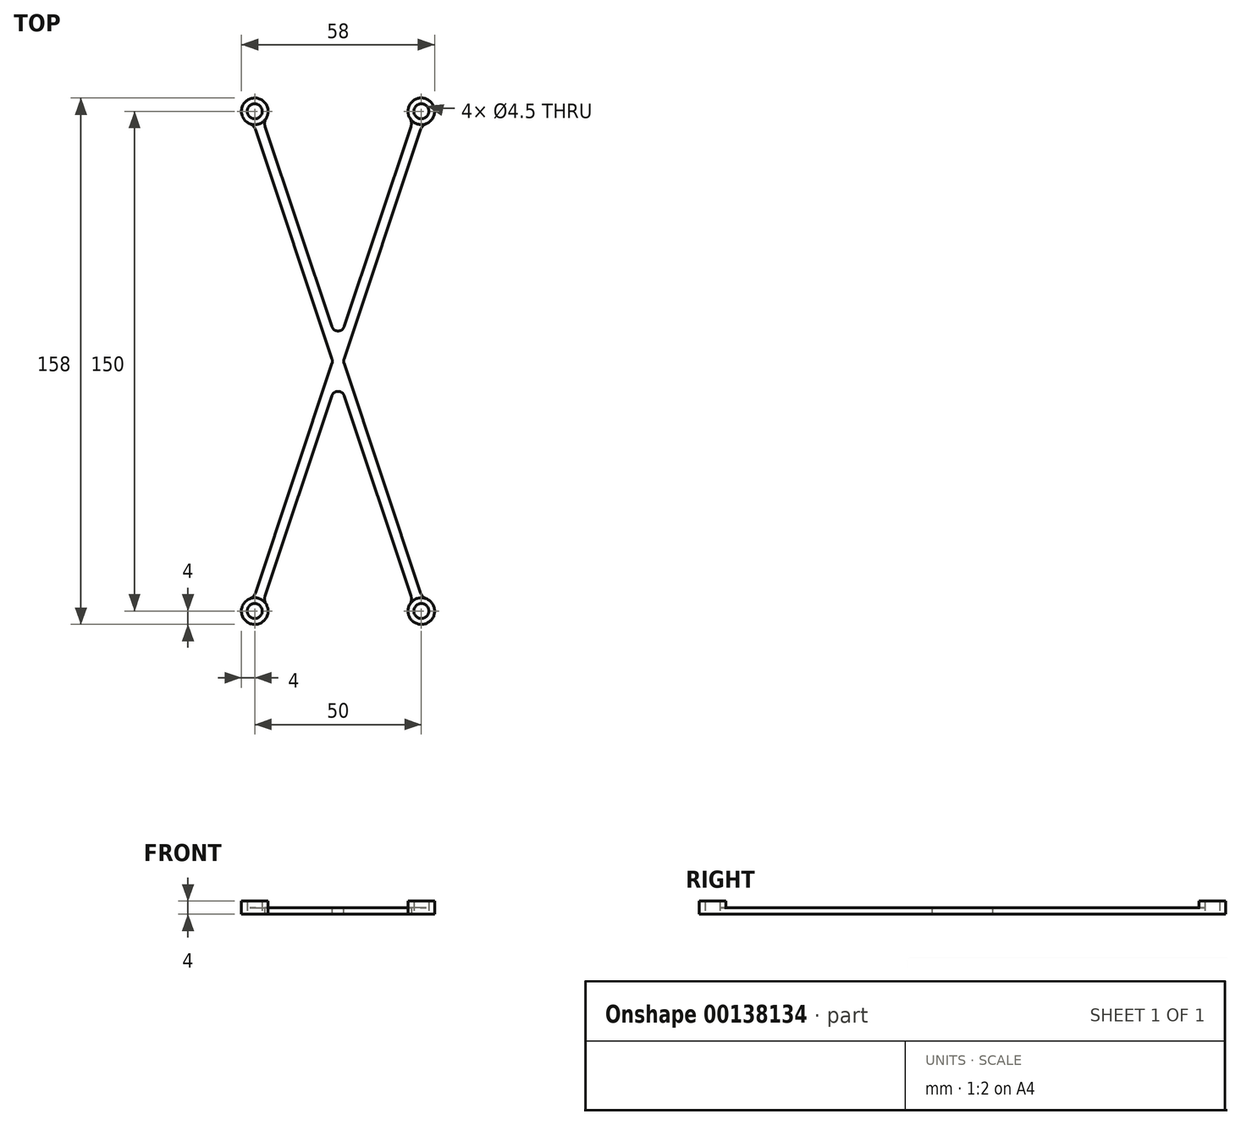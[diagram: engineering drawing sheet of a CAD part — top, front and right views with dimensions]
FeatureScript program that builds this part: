
annotation { "Feature Type Name" : "Feature", "Feature Type Description" : "" }
export const myFeature = defineFeature(function(context is Context, id is Id, definition is map)
    precondition{}
    {
        {
            var Q0;
            Q0=qCreatedBy(makeId("Top.planeOp"),FACE);
            var sketch = newSketch(context, id + "F0", { "sketchPlane" : qUnion([Q0])});
            skCircle(sketch, "E0", {"center": v(-25, 75) * mm, "radius": 2.25 * mm});
            skCircle(sketch, "E1", {"center": v(-25, 75) * mm, "radius": 4 * mm});
            skCircle(sketch, "E2.MirrorC", {"center": v(25, 75) * mm, "radius": 4 * mm});
            skCircle(sketch, "E3.MirrorC", {"center": v(25, 75) * mm, "radius": 2.25 * mm});
            skCircle(sketch, "E4.MirrorC", {"center": v(-25, -75) * mm, "radius": 4 * mm});
            skCircle(sketch, "E5.MirrorC", {"center": v(-25, -75) * mm, "radius": 2.25 * mm});
            skCircle(sketch, "E6.MirrorC", {"center": v(25, -75) * mm, "radius": 2.25 * mm});
            skCircle(sketch, "E7.MirrorC", {"center": v(25, -75) * mm, "radius": 4 * mm});
            skSolve(sketch);
        }
        {
            var Q0;
            Q0 = qSketchRegion(id + "F0", true);
            extrude(context, id + "F1", {"entities" : qUnion([Q0]), "depth" : 4 * mm});
        }
        {
            var Q0;
            Q0=qCreatedBy(makeId("Top.planeOp"),FACE);
            var sketch = newSketch(context, id + "F2", { "sketchPlane" : qUnion([Q0])});
            skLineSegment(sketch, "E8", {"start": v(-25, 75) * mm, "end": v(25, -75) * mm, "construction": true});
            skLineSegment(sketch, "E9", {"start": v(-25.46, 71.63) * mm, "end": v(22.61, -72.57) * mm});
            skLineSegment(sketch, "E10", {"start": v(-22.61, 72.57) * mm, "end": v(25.46, -71.63) * mm});
            skLineSegment(sketch, "E11", {"start": v(-25.46, 71.63) * mm, "end": v(-22.61, 72.57) * mm});
            skLineSegment(sketch, "E12", {"start": v(22.61, -72.57) * mm, "end": v(25.46, -71.63) * mm});
            skLineSegment(sketch, "E13", {"start": v(0, 0) * mm, "end": v(-23.53, -7.84) * mm, "construction": true});
            skLineSegment(sketch, "E14.MirrorCS", {"start": v(22.61, 72.57) * mm, "end": v(-25.46, -71.63) * mm});
            skLineSegment(sketch, "E15.MirrorCS", {"start": v(25.46, 71.63) * mm, "end": v(22.61, 72.57) * mm});
            skLineSegment(sketch, "E16.MirrorCS", {"start": v(25.46, 71.63) * mm, "end": v(-22.61, -72.57) * mm});
            skLineSegment(sketch, "E17.MirrorCS", {"start": v(-22.61, -72.57) * mm, "end": v(-25.46, -71.63) * mm});
            skSolve(sketch);
        }
        {
            var Q0;
            Q0 = qSketchRegion(id + "F2", true);
            extrude(context, id + "F3", {"entities" : qUnion([Q0]), "depth" : 2 * mm});
        }
        {
            var Q0;
            Q0=makeQuery(id+"F3.opExtrude","SWEPT_BODY",BODY,{"disambiguationData":[OSD([sQuery(id+"F2.wireOp",EDGE,"E9"),sQuery(id+"F2.wireOp",EDGE,"E10"),sQuery(id+"F2.wireOp",EDGE,"E11"),sQuery(id+"F2.wireOp",EDGE,"E12"),sQuery(id+"F2.wireOp",EDGE,"E14.MirrorCS"),sQuery(id+"F2.wireOp",EDGE,"E15.MirrorCS"),sQuery(id+"F2.wireOp",EDGE,"E16.MirrorCS"),sQuery(id+"F2.wireOp",EDGE,"E17.MirrorCS")])]});
            var Q1;
            Q1=makeQuery(id+"F1.opExtrude","SWEPT_BODY",BODY,{"disambiguationData":[OSD([sQuery(id+"F0.wireOp",EDGE,"E6.MirrorC"),sQuery(id+"F0.wireOp",EDGE,"E7.MirrorC")])]});
            var Q2;
            Q2=makeQuery(id+"F1.opExtrude","SWEPT_BODY",BODY,{"disambiguationData":[OSD([sQuery(id+"F0.wireOp",EDGE,"E4.MirrorC"),sQuery(id+"F0.wireOp",EDGE,"E5.MirrorC")])]});
            var Q3;
            Q3=makeQuery(id+"F1.opExtrude","SWEPT_BODY",BODY,{"disambiguationData":[OSD([sQuery(id+"F0.wireOp",EDGE,"E2.MirrorC"),sQuery(id+"F0.wireOp",EDGE,"E3.MirrorC")])]});
            var Q4;
            Q4=makeQuery(id+"F1.opExtrude","SWEPT_BODY",BODY,{"disambiguationData":[OSD([sQuery(id+"F0.wireOp",EDGE,"E0"),sQuery(id+"F0.wireOp",EDGE,"E1")])]});
            booleanBodies(context, id + "F4", {"operationType" : BooleanOperationType.UNION, "tools" : qUnion([Q0, Q1, Q2, Q3, Q4])});
        }
        {
            var Q0;
            Q0=makeQuery(id+"F3.opExtrude","SWEPT_EDGE",EDGE,{"disambiguationData":[OSD([sQuery(id+"F2.wireOp",EDGE,"E10"),sQuery(id+"F2.wireOp",EDGE,"E14.MirrorCS")])]});
            var Q1;
            Q1=makeQuery(id+"F3.opExtrude","SWEPT_EDGE",EDGE,{"disambiguationData":[OSD([sQuery(id+"F2.wireOp",EDGE,"E9"),sQuery(id+"F2.wireOp",EDGE,"E14.MirrorCS")])]});
            var Q2;
            Q2=makeQuery(id+"F3.opExtrude","SWEPT_EDGE",EDGE,{"disambiguationData":[OSD([sQuery(id+"F2.wireOp",EDGE,"E9"),sQuery(id+"F2.wireOp",EDGE,"E16.MirrorCS")])]});
            var Q3;
            Q3=makeQuery(id+"F3.opExtrude","SWEPT_EDGE",EDGE,{"disambiguationData":[OSD([sQuery(id+"F2.wireOp",EDGE,"E10"),sQuery(id+"F2.wireOp",EDGE,"E16.MirrorCS")])]});
            fillet(context, id + "F5", {"entities" : qUnion([Q0, Q1, Q2, Q3]), "radius" : 2 * mm, "tangentPropagation" : true, "allowEdgeOverflow" : false});
        }
        {
            var Q0;
            {var subQ0=sQuery(id+"F2.wireOp",EDGE,"E9");Q0=makeQuery(id+"F4.opBoolean","INTERSECT",EDGE,{"derivedFrom":[makeQuery(id+"F1.opExtrude","SWEPT_FACE",FACE,{"disambiguationData":[OSD([sQuery(id+"F0.wireOp",EDGE,"E1")])]}),makeQuery(id+"F3.opExtrude","SWEPT_FACE",FACE,{"disambiguationData":[OSD([subQ0]),TDD([makeQuery(id+"F2.imprint","IMPRINT",EDGE,{"disambiguationData":[TD([[makeQuery(id+"F2.imprint","INTERSECT",VERTEX,{"derivedFrom":[subQ0,sQuery(id+"F2.wireOp",EDGE,"E11")]}),-1.0]])],"derivedFrom":subQ0})])]})]});}
            var Q1;
            {var subQ0=sQuery(id+"F2.wireOp",EDGE,"E10");Q1=makeQuery(id+"F4.opBoolean","INTERSECT",EDGE,{"derivedFrom":[makeQuery(id+"F1.opExtrude","SWEPT_FACE",FACE,{"disambiguationData":[OSD([sQuery(id+"F0.wireOp",EDGE,"E1")])]}),makeQuery(id+"F3.opExtrude","SWEPT_FACE",FACE,{"disambiguationData":[OSD([subQ0]),TDD([makeQuery(id+"F2.imprint","IMPRINT",EDGE,{"disambiguationData":[TD([[makeQuery(id+"F2.imprint","INTERSECT",VERTEX,{"derivedFrom":[subQ0,sQuery(id+"F2.wireOp",EDGE,"E11")]}),-1.0]])],"derivedFrom":subQ0})])]})]});}
            var Q2;
            {var subQ0=sQuery(id+"F2.wireOp",EDGE,"E16.MirrorCS");Q2=makeQuery(id+"F4.opBoolean","INTERSECT",EDGE,{"derivedFrom":[makeQuery(id+"F1.opExtrude","SWEPT_FACE",FACE,{"disambiguationData":[OSD([sQuery(id+"F0.wireOp",EDGE,"E2.MirrorC")])]}),makeQuery(id+"F3.opExtrude","SWEPT_FACE",FACE,{"disambiguationData":[OSD([subQ0]),TDD([makeQuery(id+"F2.imprint","IMPRINT",EDGE,{"disambiguationData":[TD([[makeQuery(id+"F2.imprint","INTERSECT",VERTEX,{"derivedFrom":[sQuery(id+"F2.wireOp",EDGE,"E15.MirrorCS"),subQ0]}),-1.0]])],"derivedFrom":subQ0})])]})]});}
            var Q3;
            {var subQ0=sQuery(id+"F2.wireOp",EDGE,"E16.MirrorCS");Q3=makeQuery(id+"F4.opBoolean","INTERSECT",EDGE,{"derivedFrom":[makeQuery(id+"F1.opExtrude","SWEPT_FACE",FACE,{"disambiguationData":[OSD([sQuery(id+"F0.wireOp",EDGE,"E4.MirrorC")])]}),makeQuery(id+"F3.opExtrude","SWEPT_FACE",FACE,{"disambiguationData":[OSD([subQ0]),TDD([makeQuery(id+"F2.imprint","IMPRINT",EDGE,{"disambiguationData":[TD([[makeQuery(id+"F2.imprint","INTERSECT",VERTEX,{"derivedFrom":[subQ0,sQuery(id+"F2.wireOp",EDGE,"E17.MirrorCS")]}),1.0]])],"derivedFrom":subQ0})])]})]});}
            var Q4;
            {var subQ0=sQuery(id+"F2.wireOp",EDGE,"E10");Q4=makeQuery(id+"F4.opBoolean","INTERSECT",EDGE,{"derivedFrom":[makeQuery(id+"F1.opExtrude","SWEPT_FACE",FACE,{"disambiguationData":[OSD([sQuery(id+"F0.wireOp",EDGE,"E7.MirrorC")])]}),makeQuery(id+"F3.opExtrude","SWEPT_FACE",FACE,{"disambiguationData":[OSD([subQ0]),TDD([makeQuery(id+"F2.imprint","IMPRINT",EDGE,{"disambiguationData":[TD([[makeQuery(id+"F2.imprint","INTERSECT",VERTEX,{"derivedFrom":[subQ0,sQuery(id+"F2.wireOp",EDGE,"E12")]}),1.0]])],"derivedFrom":subQ0})])]})]});}
            var Q5;
            {var subQ0=sQuery(id+"F2.wireOp",EDGE,"E9");Q5=makeQuery(id+"F4.opBoolean","INTERSECT",EDGE,{"derivedFrom":[makeQuery(id+"F1.opExtrude","SWEPT_FACE",FACE,{"disambiguationData":[OSD([sQuery(id+"F0.wireOp",EDGE,"E7.MirrorC")])]}),makeQuery(id+"F3.opExtrude","SWEPT_FACE",FACE,{"disambiguationData":[OSD([subQ0]),TDD([makeQuery(id+"F2.imprint","IMPRINT",EDGE,{"disambiguationData":[TD([[makeQuery(id+"F2.imprint","INTERSECT",VERTEX,{"derivedFrom":[subQ0,sQuery(id+"F2.wireOp",EDGE,"E12")]}),1.0]])],"derivedFrom":subQ0})])]})]});}
            var Q6;
            {var subQ0=sQuery(id+"F2.wireOp",EDGE,"E14.MirrorCS");Q6=makeQuery(id+"F4.opBoolean","INTERSECT",EDGE,{"derivedFrom":[makeQuery(id+"F1.opExtrude","SWEPT_FACE",FACE,{"disambiguationData":[OSD([sQuery(id+"F0.wireOp",EDGE,"E4.MirrorC")])]}),makeQuery(id+"F3.opExtrude","SWEPT_FACE",FACE,{"disambiguationData":[OSD([subQ0]),TDD([makeQuery(id+"F2.imprint","IMPRINT",EDGE,{"disambiguationData":[TD([[makeQuery(id+"F2.imprint","INTERSECT",VERTEX,{"derivedFrom":[subQ0,sQuery(id+"F2.wireOp",EDGE,"E17.MirrorCS")]}),1.0]])],"derivedFrom":subQ0})])]})]});}
            var Q7;
            {var subQ0=sQuery(id+"F2.wireOp",EDGE,"E14.MirrorCS");Q7=makeQuery(id+"F4.opBoolean","INTERSECT",EDGE,{"derivedFrom":[makeQuery(id+"F1.opExtrude","SWEPT_FACE",FACE,{"disambiguationData":[OSD([sQuery(id+"F0.wireOp",EDGE,"E2.MirrorC")])]}),makeQuery(id+"F3.opExtrude","SWEPT_FACE",FACE,{"disambiguationData":[OSD([subQ0]),TDD([makeQuery(id+"F2.imprint","IMPRINT",EDGE,{"disambiguationData":[TD([[makeQuery(id+"F2.imprint","INTERSECT",VERTEX,{"derivedFrom":[subQ0,sQuery(id+"F2.wireOp",EDGE,"E15.MirrorCS")]}),-1.0]])],"derivedFrom":subQ0})])]})]});}
            fillet(context, id + "F6", {"entities" : qUnion([Q0, Q1, Q2, Q3, Q4, Q5, Q6, Q7]), "radius" : 3 * mm, "tangentPropagation" : true, "allowEdgeOverflow" : false});
        }
    });
